# Revit family: Haworth_Lyft_MotorDriven_Rectangle_Bench_EU_PRELIMINARY
name_source: partatom
category: Furniture
units: mm (PartAtom-declared; Revit-internal decimal feet)

## family parameters
Always vertical = Yes
Cut with Voids When Loaded = No
OmniClass Number = 23.40.70.14.64.21
OmniClass Title = Systems Furniture
Room Calculation Point = No
Shared = No
Work Plane-Based = No

## types (8) — shared parameters
Actual Height = 80 cm
Assembly Code = E2020200
Cable Finish = Haworth _ Polymer _ Undecided
Cable Height = 7 cm
Cable Tray = Yes
Cable Tray Finish = Haworth _ Paint _ Undecided _ Table
Center Cable Tray = Yes
Description = Haworth - Lyft - Motor Driven - Rectangular - Bench
Height = 80 cm
Leg Height = 76.98 cm
Manufacturer = Haworth
Max. Depth = 189.2 cm
Max. Height = 130 cm
Max. Width = 200 cm
Min. Depth = 169.2 cm
Min. Height = 65 cm
Min. Width = 140 cm
Model = A00000006
Revision Number = 0
Size = Verify Final Dim. w/ Haworth
Standard Depths = 169.2, 189.2cm
Standard Widths = 140, 160, 180, 200cm
Table Thickness = 3.02 cm
URL = https://www.haworth.com
URL - Product = https://www.haworth.com
Warranty = http://www.haworth.com
with Screen = Yes

## per-type parameters (varying)
| type | Actual Depth | Actual Width | Cable Length | Large | Small | Width |
| 160w x 169.2d | 169.2 cm | 160 cm | 120 cm | No | Yes | 160 cm |
| 180w x 189.2d | 189.2 cm | 180 cm | 140 cm | Yes | No | 180 cm |
| 140w x 189.2d | 189.2 cm | 140 cm | 100 cm | Yes | No | 140 cm |
| 200w x 169.2d | 169.2 cm | 200 cm | 160 cm | No | Yes | 200 cm |
| 200w x 189.2d | 189.2 cm | 200 cm | 160 cm | Yes | No | 200 cm |
| 140w x 169.2d | 169.2 cm | 140 cm | 100 cm | No | Yes | 140 cm |
| 160w x 189.2d | 189.2 cm | 160 cm | 120 cm | Yes | No | 160 cm |
| 180w x 169.2d | 169.2 cm | 180 cm | 140 cm | No | Yes | 180 cm |

## geometry (parser evidence)
native form markers: Sweep x22
no freeform markers — native parametric forms only
